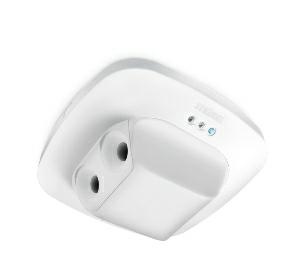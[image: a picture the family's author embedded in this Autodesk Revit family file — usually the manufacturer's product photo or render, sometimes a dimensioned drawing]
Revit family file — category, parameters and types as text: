
# Revit family: dual_us_057466
name_source: partatom
category: Elektroinstallationen
revit_build: Autodesk Revit 2016 (Build: 20190508_0715(x64)
units: mm (PartAtom-declared; Revit-internal decimal feet)

## family parameters
Basisbauteil = Fläche
Beim Laden mit Abzugskörper schneiden = Nein
Bemaßung runder Anschluss = Durchmesser verwenden
Beschriftungsausrichtung beibehalten = Nein
Gemeinsam genutzt = Nein
Raumberechnungspunkt = Nein
Teiletyp = Normal

## types (1)
- Dual US
    Apparent Load = 0 VA
    Beschreibung = Type: Presence detector; Dimensions (L x W x H): 73 x 120 x 120 mm; Mains power supply: 12 – 22,5 V; Sensor Technology: Ultrasonic; Application, place: Indoors; Application, room: corridor / aisle, Indoors; Installation site: ceiling; Installation: Concealed wiring; Electronic scalability: Yes; Mechanical scalability: No; Mounting height: 2,50 – 3,5 m; Optimum mounting height: 2,8 m; Detection angle: 360 °; Sneak-by guard: Yes; Reach, radial: 20 x 3 m (60 m²); Reach, tangential: 20 x 3 m (60 m²); Twilight setting TEACH: Yes; Twilight setting: 10 – 1000 lx; Time setting: 30 sec – 30 min; Control output, Dali: Addressable/slave; Constant-lighting control: No; Basic light level function: No; With bus coupling: Yes; Settings via: Bus; With remote control: No; Interconnection: Yes; IP-rating: IP20; Material: Plastic; Ambient temperature: -25 – +55 °C; Colour: white; Colour, RAL: 9010; Manufacturer's Warranty: 5 years; Version: DALI-2 Input Device; PU1, EAN: 4007841057466
    Height = 0 mm  [stored 0 ft]
    Hersteller = Steinel
    Length = 73 mm
    Maximum range = 10.098 m
    ModVariant = Nein
    Modell = 057466
    Mounting Place = Ceiling
    Mounting Type = Recessed
    Number of Poles = 1
    OnlyDefault = Ja
    Power Factor = 1
    Product Name = Dual US
    Product group = Presence detector
    ProductGroupID = 4
    Protection Class = Protection class
    Protection Degree = IP 20
    RlxData = <blob elided: 160285 chars, md5=63feb21b>
    Sensor characteristics = Stretched
    Sensor type = Passive (infrared)
    SensorDataFile = <blob elided: 184890 chars, md5=e609621d>
    Type of entry = Motion
    Typenbild = produkt1_057466.jpg
    Typenkommentare = Product without accessories
    URL = http://relux.com
    VarID = ---
    Voltage = 0 V
    Vorgabe-Ansicht = 1800 mm
    Weight = 0.00 kg
    Width = 120 mm  [stored 0.393701 ft]

note: [stored X ft] marks values corroborated as IEEE doubles in the binary element streams (Revit-internal decimal feet)

## geometry (parser evidence)
native form markers: Sweep x14
no freeform markers — native parametric forms only
